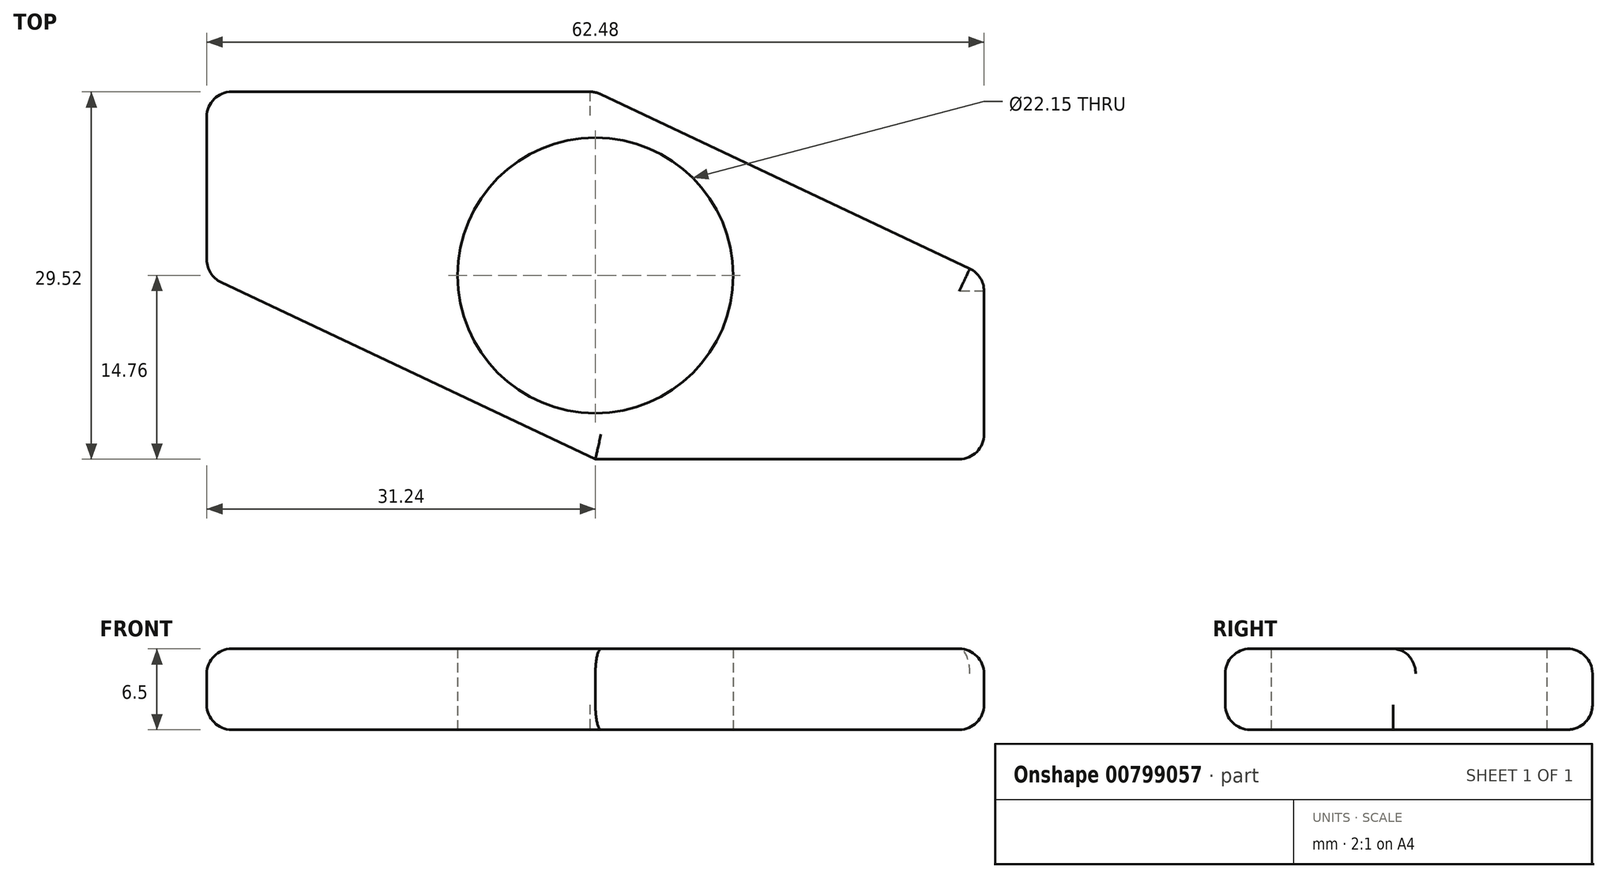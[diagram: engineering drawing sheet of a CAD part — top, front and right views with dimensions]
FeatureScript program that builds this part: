
annotation { "Feature Type Name" : "Feature", "Feature Type Description" : "" }
export const myFeature = defineFeature(function(context is Context, id is Id, definition is map)
    precondition{}
    {
        {
            var Q0;
            Q0=qCreatedBy(makeId("Top.planeOp"),FACE);
            var sketch = newSketch(context, id + "F0", { "sketchPlane" : qUnion([Q0])});
            skCircle(sketch, "E0", {"center": v(0, 0) * mm, "radius": 11.07 * mm});
            skLineSegment(sketch, "E1.bottom", {"start": v(0, 14.76) * mm, "end": v(-31.24, 14.76) * mm});
            skLineSegment(sketch, "E1.top", {"start": v(31.24, -14.76) * mm, "end": v(0, -14.76) * mm});
            skLineSegment(sketch, "E1.left", {"start": v(31.24, 0) * mm, "end": v(31.24, -14.76) * mm});
            skLineSegment(sketch, "E1.right", {"start": v(-31.24, 14.76) * mm, "end": v(-31.24, 0) * mm});
            skLineSegment(sketch, "E2", {"start": v(0, 14.76) * mm, "end": v(31.24, 0) * mm});
            skLineSegment(sketch, "E3", {"start": v(0, -14.76) * mm, "end": v(-31.24, 0) * mm});
            skPoint(sketch, "E4.orphan", {"position": v(31.24, 14.76) * mm});
            skPoint(sketch, "E5.orphan", {"position": v(-31.24, -14.76) * mm});
            skSolve(sketch);
        }
        {
            var Q0;
            Q0=makeQuery(id+"F0.imprint","IMPRINT",FACE,{"disambiguationData":[TD([[makeQuery(id+"F0.imprint","IMPRINT",EDGE,{"derivedFrom":sQuery(id+"F0.wireOp",EDGE,"E0")}),-1.0]])]});
            extrude(context, id + "F1", {"entities" : qUnion([Q0]), "depth" : 6.5 * mm, "offsetDistance" : 25 * mm});
        }
        {
            var Q0;
            Q0=makeQuery(id+"F1.opExtrude","SWEPT_EDGE",EDGE,{"disambiguationData":[OSD([sQuery(id+"F0.wireOp",EDGE,"E1.bottom"),sQuery(id+"F0.wireOp",EDGE,"E1.right")])]});
            var Q1;
            Q1=makeQuery(id+"F1.opExtrude","SWEPT_EDGE",EDGE,{"disambiguationData":[OSD([sQuery(id+"F0.wireOp",EDGE,"E1.right"),sQuery(id+"F0.wireOp",EDGE,"E3")])]});
            var Q2;
            Q2=makeQuery(id+"F1.opExtrude","CAP_EDGE",EDGE,{"disambiguationData":[OSD([sQuery(id+"F0.wireOp",EDGE,"E1.top")])],"isStart":false});
            var Q3;
            Q3=makeQuery(id+"F1.opExtrude","CAP_EDGE",EDGE,{"disambiguationData":[OSD([sQuery(id+"F0.wireOp",EDGE,"E1.top")])],"isStart":true});
            var Q4;
            Q4=makeQuery(id+"F1.opExtrude","CAP_EDGE",EDGE,{"disambiguationData":[OSD([sQuery(id+"F0.wireOp",EDGE,"E2")])],"isStart":false});
            var Q5;
            Q5=makeQuery(id+"F1.opExtrude","CAP_EDGE",EDGE,{"disambiguationData":[OSD([sQuery(id+"F0.wireOp",EDGE,"E1.bottom")])],"isStart":false});
            var Q6;
            Q6=makeQuery(id+"F1.opExtrude","CAP_EDGE",EDGE,{"disambiguationData":[OSD([sQuery(id+"F0.wireOp",EDGE,"E1.bottom")])],"isStart":true});
            var Q7;
            Q7=makeQuery(id+"F1.opExtrude","CAP_EDGE",EDGE,{"disambiguationData":[OSD([sQuery(id+"F0.wireOp",EDGE,"E1.right")])],"isStart":true});
            var Q8;
            Q8=makeQuery(id+"F1.opExtrude","CAP_EDGE",EDGE,{"disambiguationData":[OSD([sQuery(id+"F0.wireOp",EDGE,"E1.right")])],"isStart":false});
            var Q9;
            Q9=makeQuery(id+"F1.opExtrude","CAP_EDGE",EDGE,{"disambiguationData":[OSD([sQuery(id+"F0.wireOp",EDGE,"E3")])],"isStart":false});
            var Q10;
            Q10=makeQuery(id+"F1.opExtrude","CAP_EDGE",EDGE,{"disambiguationData":[OSD([sQuery(id+"F0.wireOp",EDGE,"E3")])],"isStart":true});
            var Q11;
            Q11=makeQuery(id+"F1.opExtrude","CAP_EDGE",EDGE,{"disambiguationData":[OSD([sQuery(id+"F0.wireOp",EDGE,"E1.left")])],"isStart":true});
            fillet(context, id + "F2", {"entities" : qUnion([Q0, Q1, Q2, Q3, Q4, Q5, Q6, Q7, Q8, Q9, Q10, Q11]), "radius" : 2 * mm, "tangentPropagation" : true, "allowEdgeOverflow" : false});
        }
        {
            var Q0;
            Q0=makeQuery(id+"F1.opExtrude","CAP_EDGE",EDGE,{"disambiguationData":[OSD([sQuery(id+"F0.wireOp",EDGE,"E1.left")])],"isStart":false});
            fillet(context, id + "F3", {"entities" : qUnion([Q0]), "radius" : 2 * mm, "tangentPropagation" : true, "allowEdgeOverflow" : false});
        }
    });
